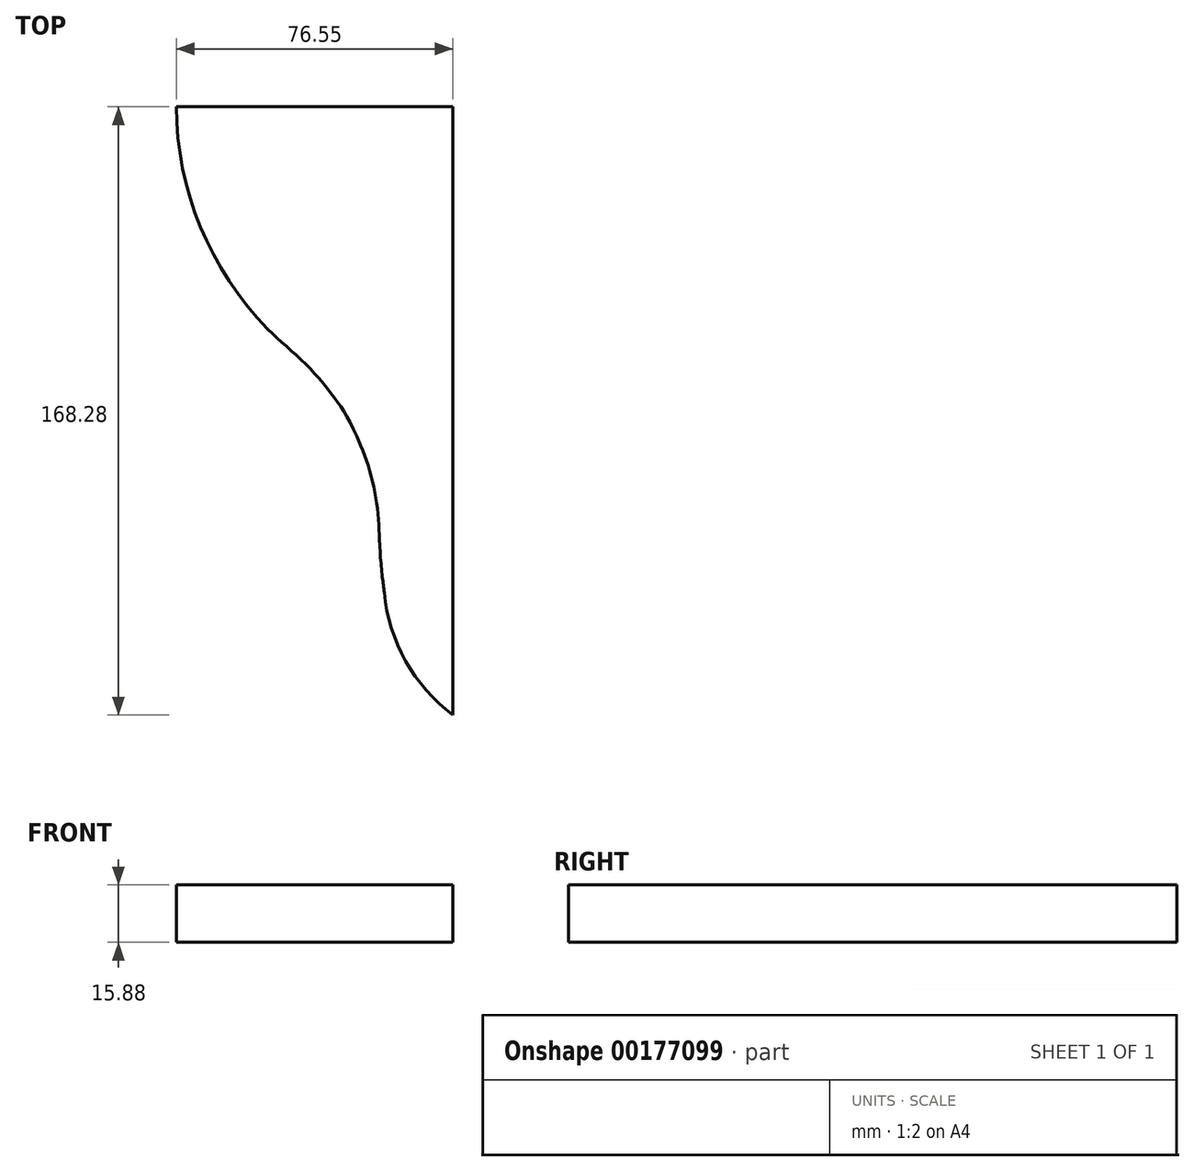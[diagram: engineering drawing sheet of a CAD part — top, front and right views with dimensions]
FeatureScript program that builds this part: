
annotation { "Feature Type Name" : "Feature", "Feature Type Description" : "" }
export const myFeature = defineFeature(function(context is Context, id is Id, definition is map)
    precondition{}
    {
        {
            var Q0;
            Q0=qCreatedBy(makeId("Top.planeOp"),FACE);
            var sketch = newSketch(context, id + "F0", { "sketchPlane" : qUnion([Q0])});
            skLineSegment(sketch, "E0", {"start": v(0, 0) * mm, "end": v(0, 168.28) * mm});
            skLineSegment(sketch, "E1", {"start": v(0, 0) * mm, "end": v(-100.95, 0) * mm, "construction": true});
            skLineSegment(sketch, "E2", {"start": v(0, 168.28) * mm, "end": v(-76.55, 168.28) * mm});
            skArc(sketch, "E3", {"start": v(-76.55, 168.27) * mm, "mid": v(-69.86, 135.05) * mm, "end": v(-51.21, 106.74) * mm});
            skFitSpline(sketch, "E4", {"points": [v(-51.21, 106.74) * mm, v(-41.29, 97.63) * mm, v(-32.84, 87.82) * mm, v(-25.53, 74.63) * mm], "startDerivative": vector(27.75, -28.38) * mm, "endDerivative": vector(25.31, -60.47) * mm});
            skArc(sketch, "E5", {"start": v(-20.44, 51.1) * mm, "mid": v(-21.9, 63.1) * mm, "end": v(-25.53, 74.63) * mm});
            skFitSpline(sketch, "E6", {"points": [v(-20.44, 51.1) * mm, v(-19.63, 38.95) * mm, v(-19.02, 33.88) * mm], "startDerivative": vector(0.66, -22.19) * mm, "endDerivative": vector(1.13, -11.56) * mm});
            skArc(sketch, "E7", {"start": v(-19.02, 33.88) * mm, "mid": v(-13.07, 14.94) * mm, "end": v(0, 0) * mm});
            skSolve(sketch);
        }
        {
            var Q0;
            Q0 = qSketchRegion(id + "F0", true);
            extrude(context, id + "F1", {"entities" : qUnion([Q0]), "depth" : 15.88 * mm});
        }
    });
